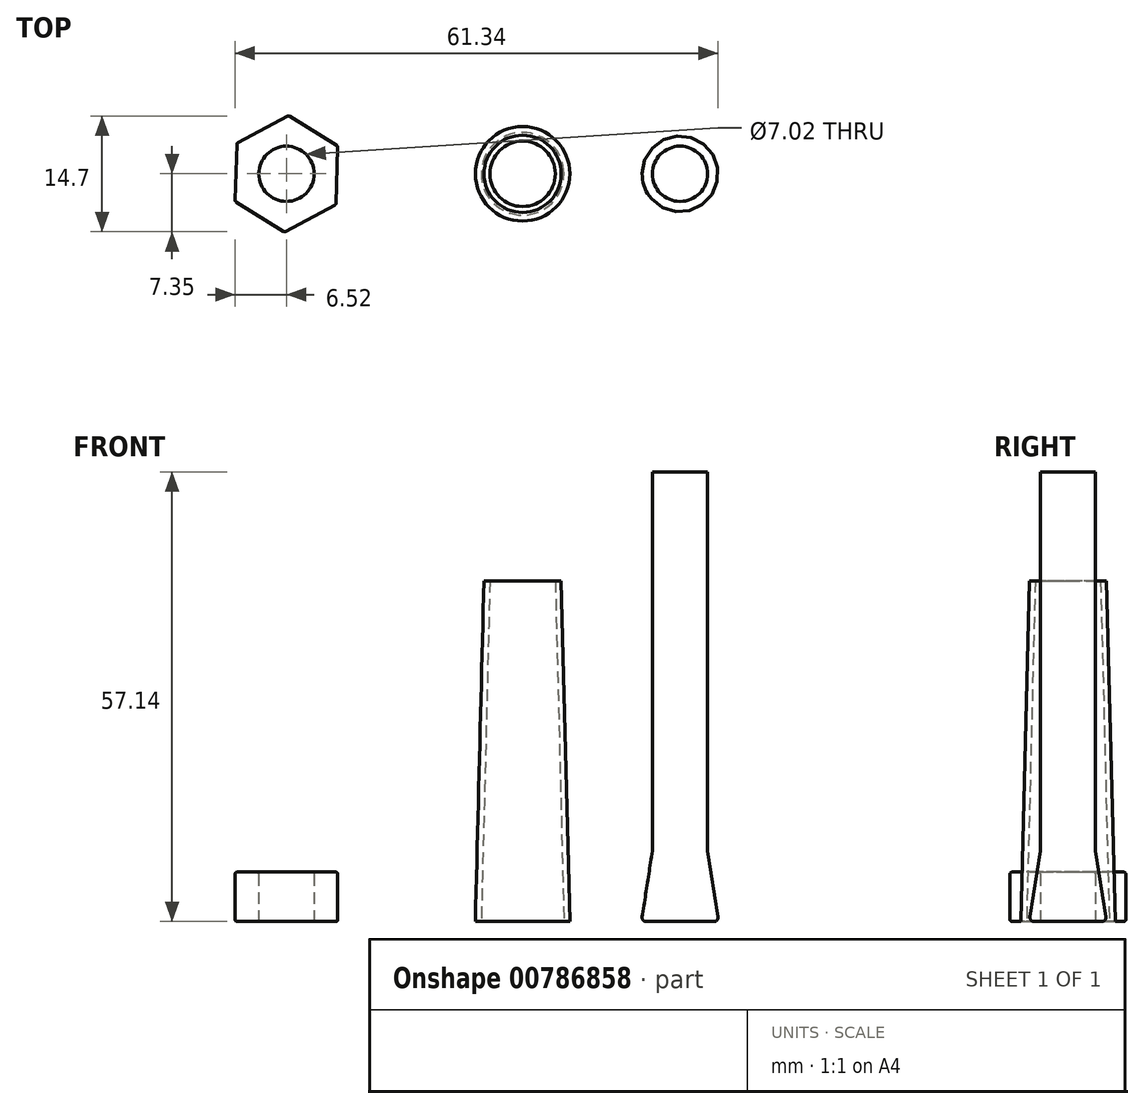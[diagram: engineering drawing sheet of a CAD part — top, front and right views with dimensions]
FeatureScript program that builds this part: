
annotation { "Feature Type Name" : "Feature", "Feature Type Description" : "" }
export const myFeature = defineFeature(function(context is Context, id is Id, definition is map)
    precondition{}
    {
        {
            var Q0;
            Q0=qCreatedBy(makeId("Top.planeOp"),FACE);
            var sketch = newSketch(context, id + "F0", { "sketchPlane" : qUnion([Q0])});
            skLineSegment(sketch, "E0", {"start": v(0, 0) * mm, "end": v(-30, 0) * mm});
            skLineSegment(sketch, "E1", {"start": v(0, 0) * mm, "end": v(30, 0) * mm});
            skSolve(sketch);
        }
        {
            var Q0;
            Q0=qCreatedBy(makeId("Front.planeOp"),FACE);
            var sketch = newSketch(context, id + "F1", { "sketchPlane" : qUnion([Q0])});
            skPoint(sketch, "E2.0", {"position": v(-30, 0) * mm});
            skLineSegment(sketch, "E3", {"start": v(-30, 0) * mm, "end": v(-30, 57.14) * mm});
            skLineSegment(sketch, "E4", {"start": v(-30, 0) * mm, "end": v(-30, 13.08) * mm});
            skLineSegment(sketch, "E5", {"start": v(-30, 0) * mm, "end": v(-25.1, 0) * mm});
            skLineSegment(sketch, "E6", {"start": v(-30, 0) * mm, "end": v(-30, 9) * mm});
            skLineSegment(sketch, "E7", {"start": v(-30, 9) * mm, "end": v(-26.49, 9) * mm});
            skLineSegment(sketch, "E8", {"start": v(-26.49, 9) * mm, "end": v(-25.1, 0) * mm});
            skLineSegment(sketch, "E9", {"start": v(-30, 57.14) * mm, "end": v(-26.49, 57.14) * mm});
            skLineSegment(sketch, "E10", {"start": v(-26.49, 57.14) * mm, "end": v(-26.49, 9) * mm});
            skSolve(sketch);
        }
        {
            var Q0;
            Q0=makeQuery(id+"F1.imprint","IMPRINT",FACE,{"disambiguationData":[TD([[makeQuery(id+"F1.imprint","IMPRINT",EDGE,{"derivedFrom":sQuery(id+"F1.wireOp",EDGE,"E3")}),-1.0]])]});
            var Q1;
            Q1=makeQuery(id+"F1.imprint","IMPRINT",FACE,{"disambiguationData":[TD([[makeQuery(id+"F1.imprint","IMPRINT",EDGE,{"derivedFrom":sQuery(id+"F1.wireOp",EDGE,"E5")}),1.0]])]});
            var Q2;
            Q2=sQuery(id+"F1.wireOp",EDGE,"E3");
            revolve(context, id + "F2", {"surfaceOperationType" : NewSurfaceOperationType.NEW, "entities" : qUnion([Q0, Q1]), "axis" : qUnion([Q2]), "revolveType" : RevolveType.FULL});
        }
        {
            var Q0;
            Q0=makeQuery(id+"F2.opRevolve","SWEPT_EDGE",EDGE,{"disambiguationData":[OSD([sQuery(id+"F1.wireOp",EDGE,"E5"),sQuery(id+"F1.wireOp",EDGE,"E8")])]});
            var Q1;
            Q1=makeQuery(id+"F2.opRevolve","SWEPT_EDGE",EDGE,{"disambiguationData":[OSD([sQuery(id+"F1.wireOp",EDGE,"E7"),sQuery(id+"F1.wireOp",EDGE,"E8"),sQuery(id+"F1.wireOp",EDGE,"E10")])]});
            fillet(context, id + "F3", {"entities" : qUnion([Q0, Q1]), "radius" : 0.5 * mm, "tangentPropagation" : true, "allowEdgeOverflow" : false});
        }
        {
            var Q0;
            Q0=qCreatedBy(makeId("Front.planeOp"),FACE);
            var sketch = newSketch(context, id + "F4", { "sketchPlane" : qUnion([Q0])});
            skLineSegment(sketch, "E11", {"start": v(0, 0) * mm, "end": v(-50, 0) * mm, "construction": true});
            skLineSegment(sketch, "E12", {"start": v(-50, 0) * mm, "end": v(-50, 43.3) * mm});
            skLineSegment(sketch, "E13", {"start": v(-50, 43.3) * mm, "end": v(-45.1, 43.3) * mm});
            skLineSegment(sketch, "E14", {"start": v(-45.1, 43.3) * mm, "end": v(-45.1, 0) * mm, "construction": true});
            skLineSegment(sketch, "E15", {"start": v(-45.1, 0) * mm, "end": v(-50, 0) * mm, "construction": true});
            skLineSegment(sketch, "E16", {"start": v(-50, 0) * mm, "end": v(-44, 0) * mm});
            skLineSegment(sketch, "E17", {"start": v(-44, 0) * mm, "end": v(-45.1, 43.3) * mm});
            skLineSegment(sketch, "E18", {"start": v(-45.1, 43.3) * mm, "end": v(-45.1, 29.8) * mm});
            skSolve(sketch);
        }
        {
            var Q0;
            Q0=makeQuery(id+"F4.imprint","IMPRINT",FACE,{"disambiguationData":[TD([[makeQuery(id+"F4.imprint","IMPRINT",EDGE,{"derivedFrom":sQuery(id+"F4.wireOp",EDGE,"E12")}),-1.0]])]});
            var Q1;
            Q1=sQuery(id+"F4.wireOp",EDGE,"E12");
            var Q2;
            Q2=sQuery(id+"F4.wireOp",EDGE,"E13");
            var Q3;
            Q3=sQuery(id+"F4.wireOp",EDGE,"E17");
            var Q4;
            Q4=sQuery(id+"F4.wireOp",EDGE,"E16");
            var Q5;
            Q5=sQuery(id+"F4.wireOp",EDGE,"E12");
            revolve(context, id + "F5", {"surfaceOperationType" : NewSurfaceOperationType.NEW, "entities" : qUnion([Q0]), "surfaceEntities" : qUnion([Q1, Q2, Q3, Q4]), "axis" : qUnion([Q5]), "revolveType" : RevolveType.FULL});
        }
        {
            var Q0;
            Q0=makeQuery(id+"F5.opRevolve","SWEPT_FACE",FACE,{"disambiguationData":[OSD([sQuery(id+"F4.wireOp",EDGE,"E13")])]});
            var Q1;
            Q1=makeQuery(id+"F5.opRevolve","SWEPT_FACE",FACE,{"disambiguationData":[OSD([sQuery(id+"F4.wireOp",EDGE,"E16")])]});
            shell(context, id + "F6", {"entities" : qUnion([Q0, Q1]), "thickness" : 0.75 * mm});
        }
        {
            var Q0;
            Q0=qCreatedBy(makeId("Top.planeOp"),FACE);
            var sketch = newSketch(context, id + "F7", { "sketchPlane" : qUnion([Q0])});
            skLineSegment(sketch, "E19", {"start": v(0, 0) * mm, "end": v(-80, 0) * mm, "construction": true});
            skCircle(sketch, "E20.cCircle", {"center": v(-80, 0) * mm, "radius": 6.4 * mm, "construction": true});
            skLineSegment(sketch, "E20.0", {"start": v(-86.28, 3.9) * mm, "end": v(-79.76, 7.4) * mm});
            skLineSegment(sketch, "E20.1", {"start": v(-79.76, 7.4) * mm, "end": v(-73.48, 3.48) * mm});
            skLineSegment(sketch, "E20.2", {"start": v(-73.48, 3.48) * mm, "end": v(-73.72, -3.9) * mm});
            skLineSegment(sketch, "E20.3", {"start": v(-73.72, -3.9) * mm, "end": v(-80.24, -7.4) * mm});
            skLineSegment(sketch, "E20.4", {"start": v(-80.24, -7.4) * mm, "end": v(-86.52, -3.48) * mm});
            skLineSegment(sketch, "E20.5", {"start": v(-86.52, -3.48) * mm, "end": v(-86.28, 3.9) * mm});
            skPoint(sketch, "E20.0.midPoint", {"position": v(-83.02, 5.65) * mm});
            skCircle(sketch, "E21", {"center": v(-80, 0) * mm, "radius": 3.5 * mm});
            skSolve(sketch);
        }
        {
            var Q0;
            Q0=makeQuery(id+"F7.imprint","IMPRINT",FACE,{"disambiguationData":[TD([[makeQuery(id+"F7.imprint","IMPRINT",EDGE,{"derivedFrom":sQuery(id+"F7.wireOp",EDGE,"E20.0")}),-1.0]])]});
            extrude(context, id + "F8", {"entities" : qUnion([Q0]), "depth" : 6.28 * mm, "offsetDistance" : 25 * mm});
        }
        {
            var Q0;
            Q0=makeQuery(id+"F8.opExtrude","CAP_FACE",FACE,{"disambiguationData":[OSD([sQuery(id+"F7.wireOp",EDGE,"E20.0"),sQuery(id+"F7.wireOp",EDGE,"E20.1"),sQuery(id+"F7.wireOp",EDGE,"E20.2"),sQuery(id+"F7.wireOp",EDGE,"E20.3"),sQuery(id+"F7.wireOp",EDGE,"E20.4"),sQuery(id+"F7.wireOp",EDGE,"E20.5"),sQuery(id+"F7.wireOp",EDGE,"E21")])],"isStart":false});
            var Q1;
            Q1=makeQuery(id+"F8.opExtrude","CAP_FACE",FACE,{"disambiguationData":[OSD([sQuery(id+"F7.wireOp",EDGE,"E20.0"),sQuery(id+"F7.wireOp",EDGE,"E20.1"),sQuery(id+"F7.wireOp",EDGE,"E20.2"),sQuery(id+"F7.wireOp",EDGE,"E20.3"),sQuery(id+"F7.wireOp",EDGE,"E20.4"),sQuery(id+"F7.wireOp",EDGE,"E20.5"),sQuery(id+"F7.wireOp",EDGE,"E21")])],"isStart":true});
            var Q2;
            Q2=makeQuery(id+"F8.opExtrude","SWEPT_FACE",FACE,{"disambiguationData":[OSD([sQuery(id+"F7.wireOp",EDGE,"E20.4")])]});
            var Q3;
            Q3=makeQuery(id+"F8.opExtrude","SWEPT_FACE",FACE,{"disambiguationData":[OSD([sQuery(id+"F7.wireOp",EDGE,"E20.3")])]});
            var Q4;
            Q4=makeQuery(id+"F8.opExtrude","SWEPT_FACE",FACE,{"disambiguationData":[OSD([sQuery(id+"F7.wireOp",EDGE,"E20.2")])]});
            var Q5;
            Q5=makeQuery(id+"F8.opExtrude","SWEPT_FACE",FACE,{"disambiguationData":[OSD([sQuery(id+"F7.wireOp",EDGE,"E20.1")])]});
            var Q6;
            Q6=makeQuery(id+"F8.opExtrude","SWEPT_FACE",FACE,{"disambiguationData":[OSD([sQuery(id+"F7.wireOp",EDGE,"E20.0")])]});
            var Q7;
            Q7=makeQuery(id+"F8.opExtrude","SWEPT_FACE",FACE,{"disambiguationData":[OSD([sQuery(id+"F7.wireOp",EDGE,"E20.5")])]});
            fillet(context, id + "F9", {"entities" : qUnion([Q0, Q1, Q2, Q3, Q4, Q5, Q6, Q7]), "radius" : 0.25 * mm, "tangentPropagation" : true, "allowEdgeOverflow" : false});
        }
    });
